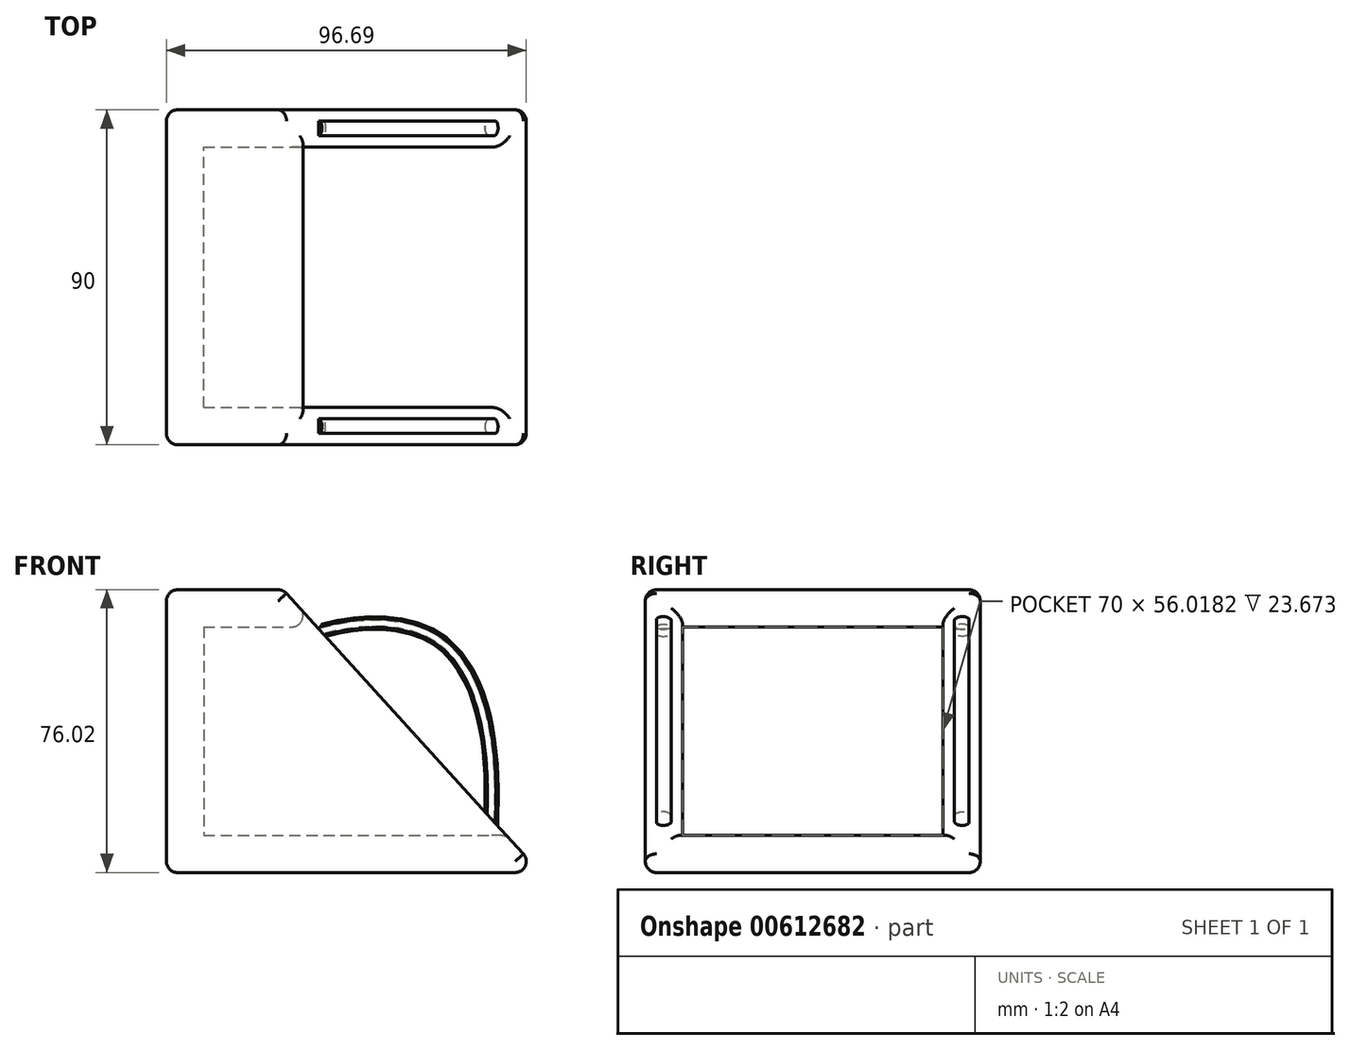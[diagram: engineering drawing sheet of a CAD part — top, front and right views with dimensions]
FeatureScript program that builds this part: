
annotation { "Feature Type Name" : "Feature", "Feature Type Description" : "" }
export const myFeature = defineFeature(function(context is Context, id is Id, definition is map)
    precondition{}
    {
        {
            var Q0;
            Q0=qCreatedBy(makeId("Front.planeOp"),FACE);
            var sketch = newSketch(context, id + "F0", { "sketchPlane" : qUnion([Q0])});
            skLineSegment(sketch, "E0", {"start": v(-45.84, 41.23) * mm, "end": v(-14.48, 41.23) * mm});
            skLineSegment(sketch, "E1", {"start": v(-45.84, 41.23) * mm, "end": v(-45.84, -34.8) * mm});
            skLineSegment(sketch, "E2", {"start": v(-45.84, -34.8) * mm, "end": v(54.63, -34.8) * mm});
            skLineSegment(sketch, "E3", {"start": v(-14.48, 41.23) * mm, "end": v(54.63, -34.8) * mm});
            skSolve(sketch);
        }
        {
            var Q0;
            Q0 = qSketchRegion(id + "F0", true);
            extrude(context, id + "F1", {"entities" : qUnion([Q0]), "depth" : 45 * mm, "offsetDistance" : 25 * mm});
        }
        {
            var Q0;
            Q0=makeQuery(id+"F1.opExtrude","SWEPT_BODY",BODY,{"disambiguationData":[OSD([sQuery(id+"F0.wireOp",EDGE,"E0"),sQuery(id+"F0.wireOp",EDGE,"E1"),sQuery(id+"F0.wireOp",EDGE,"E2"),sQuery(id+"F0.wireOp",EDGE,"E3")])]});
            var Q1;
            Q1=qCreatedBy(makeId("Front.planeOp"),FACE);
            mirror(context, id + "F2", {"operationType" : NewBodyOperationType.ADD, "entities" : qUnion([Q0]), "mirrorPlane" : qUnion([Q1])});
        }
        {
            var Q0;
            {var subQ0=makeQuery(id+"F1.opExtrude","SWEPT_FACE",FACE,{"disambiguationData":[OSD([sQuery(id+"F0.wireOp",EDGE,"E3")])]});Q0=makeQuery(id+"F2.boolean.opBoolean","MERGE",FACE,{"derivedFrom":[subQ0,makeQuery(id+"F2.opPattern","COPY",FACE,{"derivedFrom":subQ0,"instanceName":"1"})]});}
            shell(context, id + "F3", {"entities" : qUnion([Q0]), "thickness" : 10 * mm});
        }
        {
            var Q0;
            {var subQ0=makeQuery(id+"F1.opExtrude","SWEPT_FACE",FACE,{"disambiguationData":[OSD([sQuery(id+"F0.wireOp",EDGE,"E3")])]});Q0=makeQuery(id+"F2.boolean.opBoolean","MERGE",FACE,{"derivedFrom":[subQ0,makeQuery(id+"F2.opPattern","COPY",FACE,{"derivedFrom":subQ0,"instanceName":"1"})]});}
            fillet(context, id + "F4", {"entities" : qUnion([Q0]), "radius" : 3 * mm, "tangentPropagation" : true, "allowEdgeOverflow" : false});
        }
        {
            var Q0;
            Q0=makeQuery(id+"F2.opPattern","COPY",FACE,{"derivedFrom":makeQuery(id+"F1.opExtrude","CAP_FACE",FACE,{"disambiguationData":[OSD([sQuery(id+"F0.wireOp",EDGE,"E0"),sQuery(id+"F0.wireOp",EDGE,"E1"),sQuery(id+"F0.wireOp",EDGE,"E2"),sQuery(id+"F0.wireOp",EDGE,"E3")])],"isStart":false}),"instanceName":"1"});
            fillet(context, id + "F5", {"entities" : qUnion([Q0]), "radius" : 3 * mm, "tangentPropagation" : true, "allowEdgeOverflow" : false});
        }
        {
            var Q0;
            {var subQ0=makeQuery(id+"F1.opExtrude","SWEPT_FACE",FACE,{"disambiguationData":[OSD([sQuery(id+"F0.wireOp",EDGE,"E1")])]});Q0=makeQuery(id+"F2.boolean.opBoolean","MERGE",FACE,{"derivedFrom":[subQ0,makeQuery(id+"F2.opPattern","COPY",FACE,{"derivedFrom":subQ0,"instanceName":"1"})]});}
            fillet(context, id + "F6", {"entities" : qUnion([Q0]), "radius" : 3 * mm, "tangentPropagation" : true, "allowEdgeOverflow" : false});
        }
        {
            var Q0;
            {var subQ0=makeQuery(id+"F1.opExtrude","SWEPT_FACE",FACE,{"disambiguationData":[OSD([sQuery(id+"F0.wireOp",EDGE,"E2")])]});Q0=makeQuery(id+"F2.boolean.opBoolean","MERGE",FACE,{"derivedFrom":[subQ0,makeQuery(id+"F2.opPattern","COPY",FACE,{"derivedFrom":subQ0,"instanceName":"1"})]});}
            fillet(context, id + "F7", {"entities" : qUnion([Q0]), "radius" : 3 * mm, "tangentPropagation" : true, "allowEdgeOverflow" : false});
        }
        {
            var Q0;
            Q0=makeQuery(id+"F1.opExtrude","CAP_FACE",FACE,{"disambiguationData":[OSD([sQuery(id+"F0.wireOp",EDGE,"E0"),sQuery(id+"F0.wireOp",EDGE,"E1"),sQuery(id+"F0.wireOp",EDGE,"E2"),sQuery(id+"F0.wireOp",EDGE,"E3")])],"isStart":false});
            fillet(context, id + "F8", {"entities" : qUnion([Q0]), "radius" : 3 * mm, "tangentPropagation" : true, "allowEdgeOverflow" : false});
        }
        {
            var Q0;
            Q0=qCreatedBy(makeId("Front.planeOp"),FACE);
            cPlane(context, id + "F9", {"entities" : qUnion([Q0]), "cplaneType" : CPlaneType.OFFSET, "offset" : 39 * mm, "width" : 150 * mm, "height" : 150 * mm});
        }
        {
            var Q0;
            Q0=qCreatedBy(id+"F9.planeOp",FACE);
            var sketch = newSketch(context, id + "F10", { "sketchPlane" : qUnion([Q0])});
            skFitSpline(sketch, "E4", {"points": [v(-5.5, 29.78) * mm, v(8.94, 32.12) * mm, v(26.27, 28.2) * mm, v(37.2, 13.8) * mm, v(41.17, -5.8) * mm, v(41.3, -21.7) * mm], "startDerivative": vector(74.9, 17.88) * mm, "endDerivative": vector(-1.99, -80) * mm});
            skSolve(sketch);
        }
        {
            var Q0;
            {var subQ0=makeQuery(id+"F1.opExtrude","SWEPT_FACE",FACE,{"disambiguationData":[OSD([sQuery(id+"F0.wireOp",EDGE,"E3")])]});Q0=makeQuery(id+"F2.boolean.opBoolean","MERGE",FACE,{"derivedFrom":[subQ0,makeQuery(id+"F2.opPattern","COPY",FACE,{"derivedFrom":subQ0,"instanceName":"1"})]});}
            var sketch = newSketch(context, id + "F11", { "sketchPlane" : qUnion([Q0])});
            skCircle(sketch, "E5", {"center": v(-40.12, 25.44) * mm, "radius": 2.5 * mm});
            skCircle(sketch, "E6", {"center": v(-40.17, -42.91) * mm, "radius": 2.5 * mm});
            skSolve(sketch);
        }
        {
            var Q0;
            {var subQ0=sQuery(id+"F11.wireOp",EDGE,"E6");var subQ1=sQuery(id+"F0.wireOp",EDGE,"E3");var subQ2=makeQuery(id+"F1.opExtrude","SWEPT_FACE",FACE,{"disambiguationData":[OSD([subQ1])]});var subQ3=makeQuery(id+"F2.boolean.opBoolean","MERGE",FACE,{"derivedFrom":[subQ2,makeQuery(id+"F2.opPattern","COPY",FACE,{"derivedFrom":subQ2,"instanceName":"1"})]});var subQ4=makeQuery(id+"F1.opExtrude","CAP_EDGE",EDGE,{"disambiguationData":[OSD([subQ1])],"isStart":false});var subQ5=makeQuery(id+"F4.opFillet","BLEND_EDGE",EDGE,{"blendedFrom":[subQ4,subQ3],"blendedInto":[subQ3]});var subQ6=makeQuery(id+"F11.imprint","INTERSECT",VERTEX,{"disambiguationData":[OD(0.0)],"derivedFrom":[subQ5,subQ0]});Q0=makeQuery(id+"F11.imprint","IMPRINT",FACE,{"disambiguationData":[TD([[makeQuery(id+"F11.imprint","IMPRINT",EDGE,{"disambiguationData":[TD([[subQ6,1.0]])],"derivedFrom":subQ0}),1.0]])]});}
            var Q1;
            Q1=sQuery(id+"F10.wireOp",EDGE,"E4");
            sweep(context, id + "F12", {"operationType" : NewBodyOperationType.ADD, "profiles" : qUnion([Q0]), "path" : qUnion([Q1])});
        }
        {
            var Q0;
            Q0=makeQuery(id+"F1.opExtrude","SWEPT_BODY",BODY,{"disambiguationData":[OSD([sQuery(id+"F0.wireOp",EDGE,"E0"),sQuery(id+"F0.wireOp",EDGE,"E1"),sQuery(id+"F0.wireOp",EDGE,"E2"),sQuery(id+"F0.wireOp",EDGE,"E3")])]});
            var Q1;
            Q1=qCreatedBy(makeId("Front.planeOp"),FACE);
            mirror(context, id + "F13", {"operationType" : NewBodyOperationType.ADD, "entities" : qUnion([Q0]), "mirrorPlane" : qUnion([Q1])});
        }
    });
